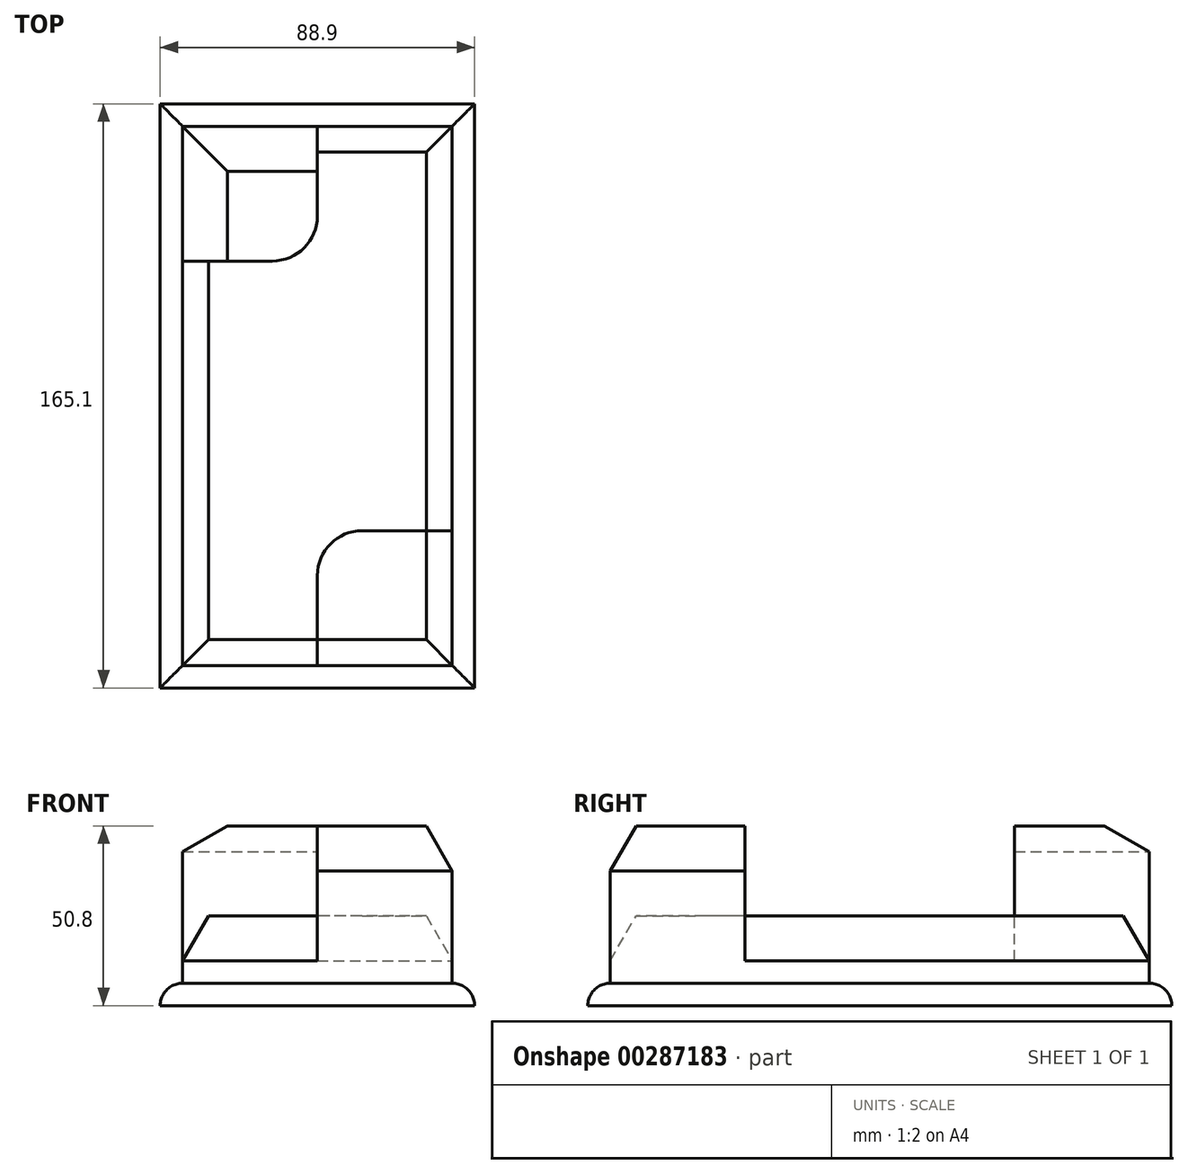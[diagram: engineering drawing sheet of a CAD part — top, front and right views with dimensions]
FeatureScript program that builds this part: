
annotation { "Feature Type Name" : "Feature", "Feature Type Description" : "" }
export const myFeature = defineFeature(function(context is Context, id is Id, definition is map)
    precondition{}
    {
        {
            var Q0;
            Q0=qCreatedBy(makeId("Top.planeOp"),FACE);
            var sketch = newSketch(context, id + "F0", { "sketchPlane" : qUnion([Q0])});
            skPoint(sketch, "E0.middle", {"position": v(0, 0) * mm});
            skLineSegment(sketch, "E1.bottom", {"start": v(38.1, 76.2) * mm, "end": v(-38.1, 76.2) * mm});
            skLineSegment(sketch, "E1.top", {"start": v(38.1, -76.2) * mm, "end": v(-38.1, -76.2) * mm});
            skLineSegment(sketch, "E1.left", {"start": v(38.1, 76.2) * mm, "end": v(38.1, -76.2) * mm});
            skLineSegment(sketch, "E1.right", {"start": v(-38.1, 76.2) * mm, "end": v(-38.1, -76.2) * mm});
            skLineSegment(sketch, "E2", {"start": v(0, 76.2) * mm, "end": v(0, 50.8) * mm});
            skLineSegment(sketch, "E3", {"start": v(-12.7, 38.1) * mm, "end": v(-38.1, 38.1) * mm});
            skLineSegment(sketch, "E4", {"start": v(0, -76.2) * mm, "end": v(0, -50.8) * mm});
            skLineSegment(sketch, "E5", {"start": v(12.7, -38.1) * mm, "end": v(38.1, -38.1) * mm});
            skPoint(sketch, "E6.visualSharp", {"position": v(0, -38.1) * mm});
            skArc(sketch, "E6.filletArc", {"start": v(12.7, -38.1) * mm, "mid": v(3.72, -41.82) * mm, "end": v(0, -50.8) * mm});
            skLineSegment(sketch, "E7.0", {"start": v(44.45, 82.55) * mm, "end": v(-44.45, 82.55) * mm});
            skLineSegment(sketch, "E7.1", {"start": v(44.45, 82.55) * mm, "end": v(44.45, -82.55) * mm});
            skLineSegment(sketch, "E7.2", {"start": v(44.45, -82.55) * mm, "end": v(-44.45, -82.55) * mm});
            skLineSegment(sketch, "E7.3", {"start": v(-44.45, 82.55) * mm, "end": v(-44.45, -82.55) * mm});
            skPoint(sketch, "E8.visualSharp", {"position": v(0, 38.1) * mm});
            skArc(sketch, "E8.filletArc", {"start": v(-12.7, 38.1) * mm, "mid": v(-3.72, 41.82) * mm, "end": v(0, 50.8) * mm});
            skSolve(sketch);
        }
        {
            var Q0;
            Q0=makeQuery(id+"F0.imprint","IMPRINT",FACE,{"disambiguationData":[TD([[makeQuery(id+"F0.imprint","IMPRINT",EDGE,{"derivedFrom":sQuery(id+"F0.wireOp",EDGE,"E7.0")}),1.0]])]});
            extrude(context, id + "F1", {"entities" : qUnion([Q0]), "depth" : 6.35 * mm});
        }
        {
            var Q0;
            {var subQ9=sQuery(id+"F0.wireOp",EDGE,"E2");Q0=makeQuery(id+"F0.imprint","IMPRINT",FACE,{"disambiguationData":[TD([[makeQuery(id+"F0.imprint","IMPRINT",EDGE,{"derivedFrom":subQ9}),1.0]])]});}
            extrude(context, id + "F2", {"entities" : qUnion([Q0]), "operationType" : NewBodyOperationType.ADD, "depth" : 25.4 * mm});
        }
        {
            var Q0;
            {var subQ1=sQuery(id+"F0.wireOp",EDGE,"E2");Q0=makeQuery(id+"F0.imprint","IMPRINT",FACE,{"disambiguationData":[TD([[makeQuery(id+"F0.imprint","IMPRINT",EDGE,{"derivedFrom":subQ1}),-1.0]])]});}
            var Q1;
            {var subQ1=sQuery(id+"F0.wireOp",EDGE,"E4");Q1=makeQuery(id+"F0.imprint","IMPRINT",FACE,{"disambiguationData":[TD([[makeQuery(id+"F0.imprint","IMPRINT",EDGE,{"derivedFrom":subQ1}),-1.0]])]});}
            extrude(context, id + "F3", {"entities" : qUnion([Q0, Q1]), "operationType" : NewBodyOperationType.ADD, "depth" : 50.8 * mm});
        }
        {
            var Q0;
            Q0=makeQuery(id+"F1.opExtrude","CAP_EDGE",EDGE,{"disambiguationData":[OSD([sQuery(id+"F0.wireOp",EDGE,"E7.1")])],"isStart":false});
            var Q1;
            Q1=makeQuery(id+"F1.opExtrude","CAP_EDGE",EDGE,{"disambiguationData":[OSD([sQuery(id+"F0.wireOp",EDGE,"E7.2")])],"isStart":false});
            var Q2;
            Q2=makeQuery(id+"F1.opExtrude","CAP_EDGE",EDGE,{"disambiguationData":[OSD([sQuery(id+"F0.wireOp",EDGE,"E7.3")])],"isStart":false});
            var Q3;
            Q3=makeQuery(id+"F1.opExtrude","CAP_EDGE",EDGE,{"disambiguationData":[OSD([sQuery(id+"F0.wireOp",EDGE,"E7.0")])],"isStart":false});
            fillet(context, id + "F4", {"entities" : qUnion([Q0, Q1, Q2, Q3]), "radius" : 6.35 * mm, "tangentPropagation" : true, "allowEdgeOverflow" : false});
        }
        {
            var Q0;
            Q0=makeQuery(id+"F2.opExtrude","CAP_EDGE",EDGE,{"disambiguationData":[OSD([sQuery(id+"F0.wireOp",EDGE,"E1.top")])],"isStart":false});
            var Q1;
            Q1=makeQuery(id+"F2.opExtrude","CAP_EDGE",EDGE,{"disambiguationData":[OSD([sQuery(id+"F0.wireOp",EDGE,"E1.right")])],"isStart":false});
            var Q2;
            Q2=makeQuery(id+"F2.opExtrude","CAP_EDGE",EDGE,{"disambiguationData":[OSD([sQuery(id+"F0.wireOp",EDGE,"E1.left")])],"isStart":false});
            var Q3;
            Q3=makeQuery(id+"F2.opExtrude","CAP_EDGE",EDGE,{"disambiguationData":[OSD([sQuery(id+"F0.wireOp",EDGE,"E1.bottom")])],"isStart":false});
            var Q4;
            Q4=makeQuery(id+"F3.opExtrude","CAP_EDGE",EDGE,{"disambiguationData":[OSD([sQuery(id+"F0.wireOp",EDGE,"E1.right")])],"isStart":false});
            var Q5;
            Q5=makeQuery(id+"F3.opExtrude","CAP_EDGE",EDGE,{"disambiguationData":[OSD([sQuery(id+"F0.wireOp",EDGE,"E1.bottom")])],"isStart":false});
            var Q6;
            Q6=makeQuery(id+"F3.opExtrude","CAP_EDGE",EDGE,{"disambiguationData":[OSD([sQuery(id+"F0.wireOp",EDGE,"E1.top")])],"isStart":false});
            var Q7;
            Q7=makeQuery(id+"F3.opExtrude","CAP_EDGE",EDGE,{"disambiguationData":[OSD([sQuery(id+"F0.wireOp",EDGE,"E1.left")])],"isStart":false});
            chamfer(context, id + "F5", {"entities" : qUnion([Q0, Q1, Q2, Q3, Q4, Q5, Q6, Q7]), "chamferType" : ChamferType.OFFSET_ANGLE, "width" : 12.7 * mm, "oppositeDirection" : false, "angle" : 30 * degree, "tangentPropagation" : true});
        }
    });
